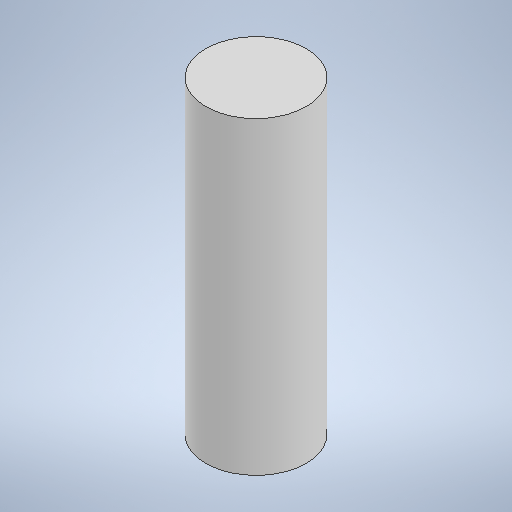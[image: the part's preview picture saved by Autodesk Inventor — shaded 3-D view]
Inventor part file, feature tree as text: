
AUTODESK INVENTOR PART (.ipt)
format: ipt  version: 2025.1 (Build 291241000, 241)  size: 220,672 bytes
history: native  units: mm
features: extrude x1, sketch x1
ambient origin geometry x8: Origin, YZ Plane, XZ Plane, XY Plane, X Axis, Y Axis, Z Axis, Center Point
bodies: Solid1 (feature_tree)
feature tree (2):
  extrude  "Extrusion1"  Depth=8.0mm TaperAngle=0.0deg
  sketch  "Sketch1"  dims[d0=2.6mm d1=8.0mm d2=0.0mm]
